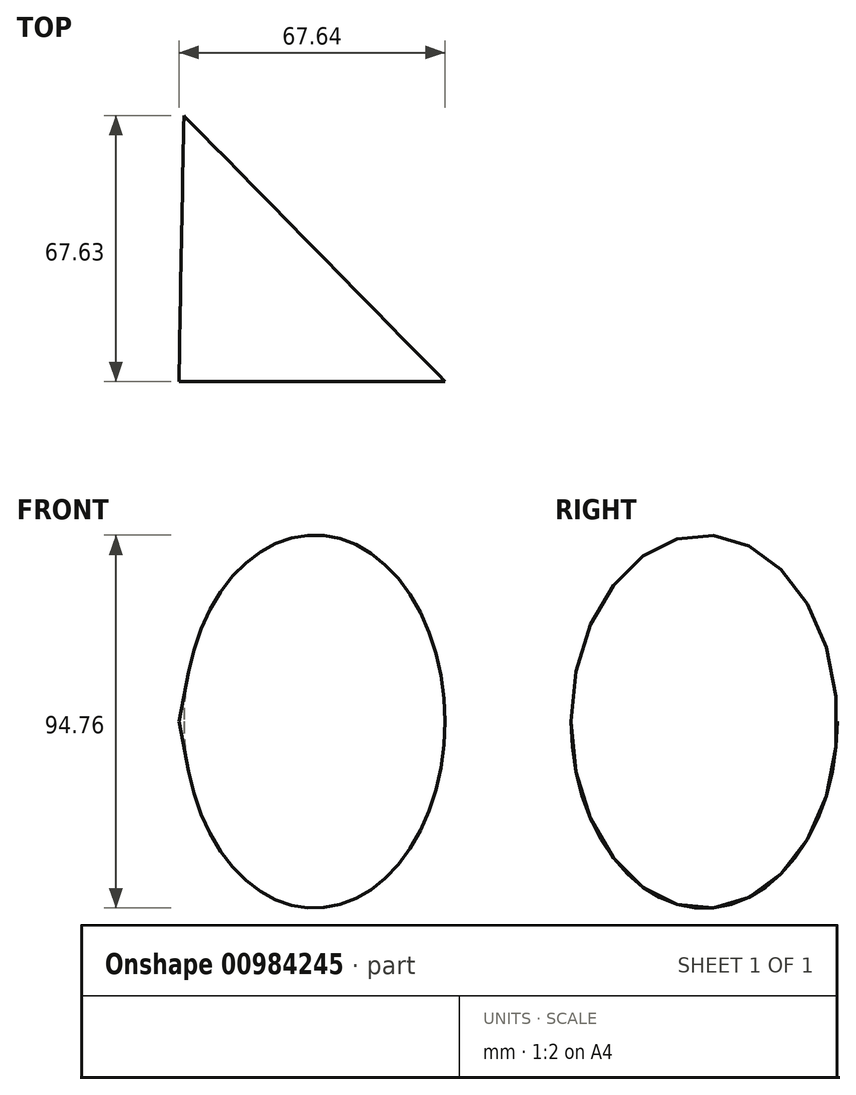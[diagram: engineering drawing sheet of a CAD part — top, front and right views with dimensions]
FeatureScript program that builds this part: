
annotation { "Feature Type Name" : "Feature", "Feature Type Description" : "" }
export const myFeature = defineFeature(function(context is Context, id is Id, definition is map)
    precondition{}
    {
        {
            var Q0;
            Q0=qCreatedBy(makeId("Top.planeOp"),FACE);
            var sketch = newSketch(context, id + "F0", { "sketchPlane" : qUnion([Q0])});
            skLineSegment(sketch, "E0", {"start": v(67.64, 0) * mm, "end": v(0, 0) * mm});
            skLineSegment(sketch, "E1", {"start": v(0, 0) * mm, "end": v(52.18, 51.23) * mm});
            skArc(sketch, "E2", {"start": v(67.64, 0) * mm, "mid": v(102.28, 38.4) * mm, "end": v(52.18, 51.23) * mm});
            skSolve(sketch);
        }
        {
            var Q0;
            Q0=makeQuery(id+"F0.imprint","IMPRINT",FACE,{"disambiguationData":[TD([[makeQuery(id+"F0.imprint","IMPRINT",EDGE,{"derivedFrom":sQuery(id+"F0.wireOp",EDGE,"E0")}),-1.0]])]});
            var Q1;
            Q1=sQuery(id+"F0.wireOp",EDGE,"E1");
            revolve(context, id + "F1", {"surfaceOperationType" : NewSurfaceOperationType.NEW, "entities" : qUnion([Q0]), "axis" : qUnion([Q1]), "revolveType" : RevolveType.FULL});
        }
    });
